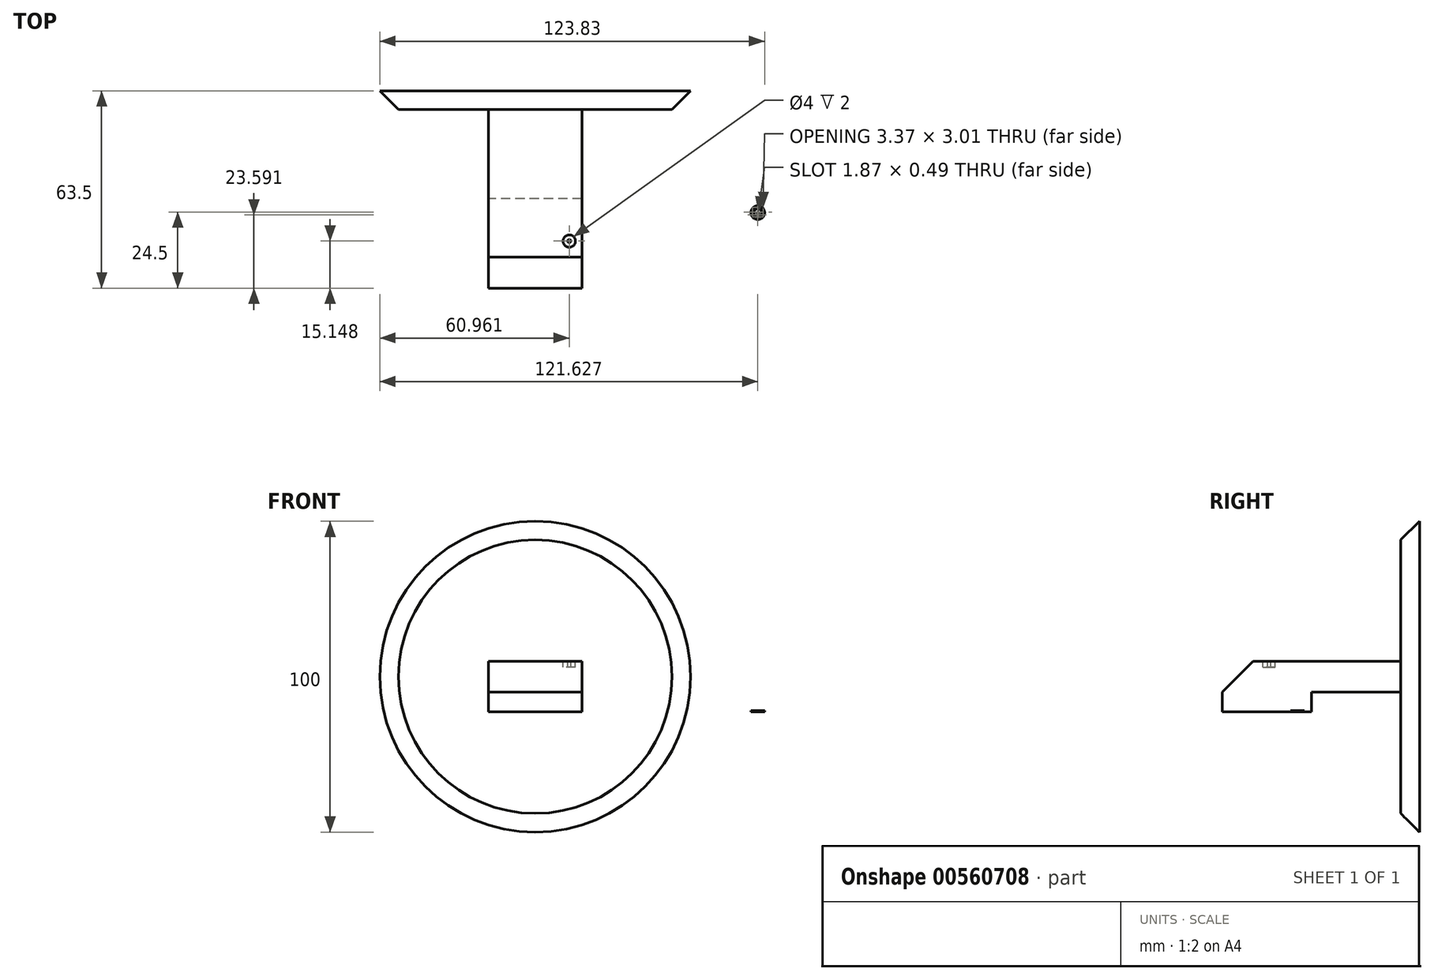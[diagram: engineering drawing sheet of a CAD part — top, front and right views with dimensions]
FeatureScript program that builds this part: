
annotation { "Feature Type Name" : "Feature", "Feature Type Description" : "" }
export const myFeature = defineFeature(function(context is Context, id is Id, definition is map)
    precondition{}
    {
        {
            var Q0;
            Q0=qCreatedBy(makeId("Front.planeOp"),FACE);
            var sketch = newSketch(context, id + "F0", { "sketchPlane" : qUnion([Q0])});
            skCircle(sketch, "E0", {"center": v(-39.62, 33.1) * mm, "radius": 50 * mm});
            skSolve(sketch);
        }
        {
            var Q0;
            Q0=makeQuery(id+"F0.imprint","IMPRINT",FACE,{"disambiguationData":[TD([[makeQuery(id+"F0.imprint","IMPRINT",EDGE,{"derivedFrom":sQuery(id+"F0.wireOp",EDGE,"E0")}),1.0]])]});
            extrude(context, id + "F1", {"entities" : qUnion([Q0]), "depth" : 6 * mm, "offsetDistance" : 25 * mm});
        }
        {
            var Q0;
            Q0=makeQuery(id+"F1.opExtrude","CAP_EDGE",EDGE,{"disambiguationData":[OSD([sQuery(id+"F0.wireOp",EDGE,"E0")])],"isStart":false});
            chamfer(context, id + "F2", {"entities" : qUnion([Q0]), "width" : 6 * mm, "tangentPropagation" : true});
        }
        {
            var Q0;
            Q0=makeQuery(id+"F1.opExtrude","CAP_FACE",FACE,{"disambiguationData":[OSD([sQuery(id+"F0.wireOp",EDGE,"E0")])],"isStart":false});
            var sketch = newSketch(context, id + "F3", { "sketchPlane" : qUnion([Q0])});
            skPoint(sketch, "E1.center.orphan", {"position": v(-39.62, 33.1) * mm});
            skPoint(sketch, "E2.start.orphan", {"position": v(-39.62, 43.1) * mm});
            skPoint(sketch, "E3.start.orphan", {"position": v(-24.62, 23.1) * mm});
            skPoint(sketch, "E4.start.orphan", {"position": v(-24.62, 43.1) * mm});
            skLineSegment(sketch, "E5", {"start": v(-39.62, 28.1) * mm, "end": v(-24.62, 28.1) * mm});
            skLineSegment(sketch, "E6", {"start": v(-24.62, 28.1) * mm, "end": v(-24.62, 38.1) * mm});
            skLineSegment(sketch, "E7", {"start": v(-24.62, 38.1) * mm, "end": v(-39.62, 38.1) * mm});
            skLineSegment(sketch, "E8", {"start": v(-39.62, 38.1) * mm, "end": v(-54.62, 38.1) * mm});
            skLineSegment(sketch, "E9", {"start": v(-54.62, 38.1) * mm, "end": v(-54.62, 28.1) * mm});
            skLineSegment(sketch, "E10", {"start": v(-54.62, 28.1) * mm, "end": v(-39.62, 28.1) * mm});
            skSolve(sketch);
        }
        {
            var Q0;
            Q0=makeQuery(id+"F3.imprint","IMPRINT",FACE,{"disambiguationData":[TD([[makeQuery(id+"F3.imprint","IMPRINT",EDGE,{"derivedFrom":sQuery(id+"F3.wireOp",EDGE,"E5")}),1.0]])]});
            extrude(context, id + "F4", {"entities" : qUnion([Q0]), "operationType" : NewBodyOperationType.ADD, "depth" : 57.5 * mm, "offsetDistance" : 25 * mm});
        }
        {
            var Q0;
            Q0=makeQuery(id+"F4.opExtrude","SWEPT_FACE",FACE,{"disambiguationData":[OSD([sQuery(id+"F3.wireOp",EDGE,"E5"),sQuery(id+"F3.wireOp",EDGE,"E10")])]});
            var sketch = newSketch(context, id + "F5", { "sketchPlane" : qUnion([Q0])});
            skPoint(sketch, "E11.firstSnap0", {"position": v(-54.62, 34.75) * mm});
            skPoint(sketch, "E11.firstSnap1", {"position": v(-39.62, 63.5) * mm});
            skLineSegment(sketch, "E11.bottom", {"start": v(-39.62, 34.75) * mm, "end": v(-119.62, 34.75) * mm});
            skLineSegment(sketch, "E11.top", {"start": v(-39.62, 124.75) * mm, "end": v(-119.62, 124.75) * mm});
            skLineSegment(sketch, "E11.left", {"start": v(-39.62, 34.75) * mm, "end": v(-39.62, 63.5) * mm});
            skLineSegment(sketch, "E11.right", {"start": v(-119.62, 34.75) * mm, "end": v(-119.62, 124.75) * mm});
            skLineSegment(sketch, "E12.bottom", {"start": v(-39.62, 34.75) * mm, "end": v(40.38, 34.75) * mm});
            skLineSegment(sketch, "E12.top", {"start": v(-39.62, 124.75) * mm, "end": v(40.38, 124.75) * mm});
            skLineSegment(sketch, "E12.right", {"start": v(40.38, 34.75) * mm, "end": v(40.38, 124.75) * mm});
            skLineSegment(sketch, "E13", {"start": v(-54.62, 34.75) * mm, "end": v(-24.62, 34.75) * mm});
            skSolve(sketch);
        }
        {
            var Q0;
            {var subQ9=sQuery(id+"F5.wireOp",EDGE,"E11.bottom");Q0=makeQuery(id+"F5.imprint","IMPRINT",FACE,{"disambiguationData":[TD([[makeQuery(id+"F5.imprint","IMPRINT",EDGE,{"derivedFrom":subQ9}),-1.0]])]});}
            var Q1;
            {var subQ0=sQuery(id+"F5.wireOp",EDGE,"E11.left");Q1=makeQuery(id+"F5.imprint","IMPRINT",FACE,{"disambiguationData":[TD([[makeQuery(id+"F5.imprint","IMPRINT",EDGE,{"derivedFrom":subQ0}),-1.0]])]});}
            var Q2;
            {var subQ0=sQuery(id+"F5.wireOp",EDGE,"E11.left");Q2=makeQuery(id+"F5.imprint","IMPRINT",FACE,{"disambiguationData":[TD([[makeQuery(id+"F5.imprint","IMPRINT",EDGE,{"derivedFrom":subQ0}),1.0]])]});}
            extrude(context, id + "F6", {"entities" : qUnion([Q0, Q1, Q2]), "operationType" : NewBodyOperationType.ADD, "depth" : 6 * mm, "offsetDistance" : 25 * mm});
        }
        {
            var Q0;
            Q0=makeQuery(id+"F6.opExtrude","CAP_FACE",FACE,{"disambiguationData":[OSD([sQuery(id+"F5.wireOp",EDGE,"E11.bottom"),sQuery(id+"F5.wireOp",EDGE,"E11.top"),sQuery(id+"F5.wireOp",EDGE,"E11.right"),sQuery(id+"F5.wireOp",EDGE,"E12.bottom"),sQuery(id+"F5.wireOp",EDGE,"E12.top"),sQuery(id+"F5.wireOp",EDGE,"E12.right"),sQuery(id+"F5.wireOp",EDGE,"E13")])],"isStart":false});
            var sketch = newSketch(context, id + "F7", { "sketchPlane" : qUnion([Q0])});
            skLineSegment(sketch, "E14", {"start": v(37.38, 43.56) * mm, "end": v(37.38, 121.56) * mm});
            skLineSegment(sketch, "E15", {"start": v(37.38, 121.56) * mm, "end": v(-116.62, 121.56) * mm});
            skLineSegment(sketch, "E16", {"start": v(-116.62, 121.56) * mm, "end": v(-116.62, 43.56) * mm});
            skLineSegment(sketch, "E17", {"start": v(-116.62, 43.56) * mm, "end": v(37.38, 43.56) * mm});
            skPoint(sketch, "E18.start.orphan", {"position": v(40.38, 43.56) * mm});
            skPoint(sketch, "E19.end.orphan", {"position": v(33.66, 43.56) * mm});
            skSolve(sketch);
        }
        {
            var Q0;
            Q0=makeQuery(id+"F7.imprint","IMPRINT",FACE,{"disambiguationData":[TD([[makeQuery(id+"F7.imprint","IMPRINT",EDGE,{"derivedFrom":sQuery(id+"F7.wireOp",EDGE,"E14")}),1.0]])]});
            extrude(context, id + "F8", {"entities" : qUnion([Q0]), "operationType" : NewBodyOperationType.REMOVE, "oppositeDirection" : true, "depth" : 1 * mm, "offsetDistance" : 25 * mm});
        }
        {
            var Q0;
            Q0=makeQuery(id+"F4.opExtrude","CAP_EDGE",EDGE,{"disambiguationData":[OSD([sQuery(id+"F3.wireOp",EDGE,"E7"),sQuery(id+"F3.wireOp",EDGE,"E8")])],"isStart":false});
            chamfer(context, id + "F9", {"entities" : qUnion([Q0]), "width" : 10 * mm, "tangentPropagation" : true});
        }
        {
            var Q0;
            Q0=makeQuery(id+"F6.opExtrude","CAP_FACE",FACE,{"disambiguationData":[OSD([sQuery(id+"F5.wireOp",EDGE,"E11.bottom"),sQuery(id+"F5.wireOp",EDGE,"E11.top"),sQuery(id+"F5.wireOp",EDGE,"E11.right"),sQuery(id+"F5.wireOp",EDGE,"E12.bottom"),sQuery(id+"F5.wireOp",EDGE,"E12.top"),sQuery(id+"F5.wireOp",EDGE,"E12.right"),sQuery(id+"F5.wireOp",EDGE,"E13")])],"isStart":false});
            var sketch = newSketch(context, id + "F10", { "sketchPlane" : qUnion([Q0])});
            skCircle(sketch, "E20", {"center": v(32, 39.22) * mm, "radius": 2.2 * mm});
            skArc(sketch, "E21", {"start": v(30.8, 40.43) * mm, "mid": v(32, 37.5) * mm, "end": v(33.22, 40.43) * mm});
            skArc(sketch, "E22", {"start": v(31.13, 40.09) * mm, "mid": v(32, 37.98) * mm, "end": v(32.88, 40.09) * mm});
            skArc(sketch, "E23", {"start": v(33.22, 40.43) * mm, "mid": v(32.88, 40.43) * mm, "end": v(32.88, 40.09) * mm});
            skArc(sketch, "E24", {"start": v(31.13, 40.09) * mm, "mid": v(31.13, 40.43) * mm, "end": v(30.8, 40.43) * mm});
            skArc(sketch, "E25", {"start": v(31.76, 39.22) * mm, "mid": v(32, 38.97) * mm, "end": v(32.25, 39.22) * mm});
            skLineSegment(sketch, "E26", {"start": v(32.25, 39.22) * mm, "end": v(32.25, 40.6) * mm});
            skLineSegment(sketch, "E27", {"start": v(31.76, 39.22) * mm, "end": v(31.76, 40.6) * mm});
            skArc(sketch, "E28", {"start": v(32.25, 40.6) * mm, "mid": v(32, 40.84) * mm, "end": v(31.76, 40.6) * mm});
            skArc(sketch, "E29", {"start": v(24.14, 36.34) * mm, "mid": v(27.02, 39.22) * mm, "end": v(24.14, 42.1) * mm});
            skPoint(sketch, "E30.center.orphan", {"position": v(7.92, 39.22) * mm});
            skArc(sketch, "E31", {"start": v(7.92, 42.1) * mm, "mid": v(5.04, 39.22) * mm, "end": v(7.92, 36.34) * mm});
            skLineSegment(sketch, "E32", {"start": v(7.92, 36.34) * mm, "end": v(24.14, 36.34) * mm});
            skLineSegment(sketch, "E33", {"start": v(24.14, 42.1) * mm, "end": v(7.92, 42.1) * mm});
            skLineSegment(sketch, "E34", {"start": v(16.03, 42.1) * mm, "end": v(16.03, 36.34) * mm});
            skSolve(sketch);
        }
        {
            var Q0;
            Q0=makeQuery(id+"F10.imprint","IMPRINT",FACE,{"disambiguationData":[TD([[makeQuery(id+"F10.imprint","IMPRINT",EDGE,{"derivedFrom":sQuery(id+"F10.wireOp",EDGE,"E20")}),1.0]])]});
            extrude(context, id + "F11", {"entities" : qUnion([Q0]), "operationType" : NewBodyOperationType.ADD, "depth" : 0.3 * mm, "offsetDistance" : 25 * mm});
        }
        {
            var Q0;
            Q0=makeQuery(id+"F11.boolean.opBoolean","SPLIT",FACE,{"disambiguationData":[TD([makeQuery(id+"F11.opExtrude","SWEPT_FACE",FACE,{"disambiguationData":[OSD([sQuery(id+"F10.wireOp",EDGE,"E25")])]})])],"derivedFrom":makeQuery(id+"F6.opExtrude","CAP_FACE",FACE,{"disambiguationData":[OSD([sQuery(id+"F5.wireOp",EDGE,"E11.bottom"),sQuery(id+"F5.wireOp",EDGE,"E11.top"),sQuery(id+"F5.wireOp",EDGE,"E11.right"),sQuery(id+"F5.wireOp",EDGE,"E12.bottom"),sQuery(id+"F5.wireOp",EDGE,"E12.top"),sQuery(id+"F5.wireOp",EDGE,"E12.right"),sQuery(id+"F5.wireOp",EDGE,"E13")])],"isStart":false})});
            var Q1;
            Q1=makeQuery(id+"F11.boolean.opBoolean","SPLIT",FACE,{"disambiguationData":[TD([makeQuery(id+"F11.opExtrude","SWEPT_FACE",FACE,{"disambiguationData":[OSD([sQuery(id+"F10.wireOp",EDGE,"E21")])]})])],"derivedFrom":makeQuery(id+"F6.opExtrude","CAP_FACE",FACE,{"disambiguationData":[OSD([sQuery(id+"F5.wireOp",EDGE,"E11.bottom"),sQuery(id+"F5.wireOp",EDGE,"E11.top"),sQuery(id+"F5.wireOp",EDGE,"E11.right"),sQuery(id+"F5.wireOp",EDGE,"E12.bottom"),sQuery(id+"F5.wireOp",EDGE,"E12.top"),sQuery(id+"F5.wireOp",EDGE,"E12.right"),sQuery(id+"F5.wireOp",EDGE,"E13")])],"isStart":false})});
            extrude(context, id + "F12", {"entities" : qUnion([Q0, Q1]), "operationType" : NewBodyOperationType.ADD, "depth" : 0.35 * mm, "offsetDistance" : 25 * mm});
        }
        {
            var Q0;
            Q0=makeQuery(id+"F4.opExtrude","SWEPT_FACE",FACE,{"disambiguationData":[OSD([sQuery(id+"F3.wireOp",EDGE,"E7"),sQuery(id+"F3.wireOp",EDGE,"E8")])]});
            var sketch = newSketch(context, id + "F13", { "sketchPlane" : qUnion([Q0])});
            skCircle(sketch, "E35", {"center": v(-28.66, -48.35) * mm, "radius": 0.5 * mm});
            skCircle(sketch, "E36", {"center": v(-28.66, -48.35) * mm, "radius": 2 * mm});
            skLineSegment(sketch, "E37", {"start": v(-42.64, -49.37) * mm, "end": v(-48.64, -49.37) * mm});
            skLineSegment(sketch, "E38", {"start": v(-48.64, -49.37) * mm, "end": v(-48.24, -47.92) * mm});
            skLineSegment(sketch, "E39", {"start": v(-42.64, -49.37) * mm, "end": v(-43.05, -47.92) * mm});
            skLineSegment(sketch, "E40", {"start": v(-48.24, -47.92) * mm, "end": v(-43.05, -47.92) * mm});
            skSolve(sketch);
        }
        {
            var Q0;
            Q0=makeQuery(id+"F13.imprint","IMPRINT",FACE,{"disambiguationData":[TD([[makeQuery(id+"F13.imprint","IMPRINT",EDGE,{"derivedFrom":sQuery(id+"F13.wireOp",EDGE,"E35")}),-1.0]])]});
            extrude(context, id + "F14", {"entities" : qUnion([Q0]), "operationType" : NewBodyOperationType.REMOVE, "oppositeDirection" : true, "depth" : 2 * mm, "offsetDistance" : 25 * mm});
        }
    });
